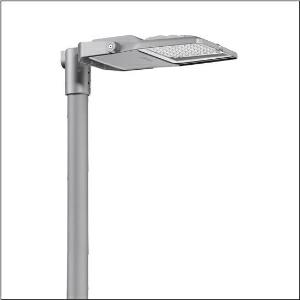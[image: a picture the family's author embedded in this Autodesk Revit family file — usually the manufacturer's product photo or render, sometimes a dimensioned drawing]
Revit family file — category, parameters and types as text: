
# Revit family: floodlight_fl_21_mini___pl61_5xa7775c2c3a_8aba
name_source: partatom
category: Lighting Fixtures
units: mm (PartAtom-declared; Revit-internal decimal feet)

## family parameters
Cut with Voids When Loaded = No
Host = Face
Light Source = No
Part Type = Normal
Room Calculation Point = No
Round Connector Dimension = Use Diameter
Shared = No

## types (1)
- --- (1 x LED, 11960 lm, 89 W, 3000K)
    Apparent Load = 89 VA
    CIE Flux Codes = 33 65 98 100 100
    Color Rendering = 70
    Color Temperature = 3000K
    Default Elevation = 1800 mm
    Description = Floodlight FL 21 mini, floodlight, primary light control with lens, of PMMA, primary optical cover: protective disc, of toughened safety glass, transparent, light distribution: PL61, light emission: direct distribution, installation type: surface-mounted, LED, High Power LED, rated luminous flux: 11.960lm, luminous efficacy: 134lm/W, light colour: 730, colour temperature: 3000K, control: flexible luminous flux parameterisation, time-dependent luminous flux control, constant luminous flux control, overheat protection, pre-setting: logarithmic dimming characteristic, with terminal, 6-pole, mains connection: 220..240V, AC, 50/60Hz, start of lifetime: 89W, end of service life: 94W, reduction: 43W, luminaire housing, of diecast aluminium, powder-coated, Siteco® metallic grey (DB 702S), corrosivity category C5 mid according to DIN EN ISO 12944, sealing non-destructively replaceable, please order mast flange separately, mast bracket, of steel, galvanised, powder-coated, Siteco® metallic grey (DB 702S), Smart Interface above, protection rating (complete): IP66, insulation class (complete): insulation class II (safety insulation), certification: CE, ENEC, VDE, protection symbol: D, impact resistance: IK08, permissible operating ambient temperature: -40..+40°C, permissible operating ambient temperature for outdoor applications: -40..+50°C, standard: DIN EN 12944, LABS conformity tested according to VDMA 24364:2018-05, packaging unit: 1 piece

Light Distribution: PL61
    Height = 70 mm
    Lamp = 1 x LED
    Lamp Light Flux = 11960 lm
    Lamp Power = 89 W
    Lamp count = 1
    Length = 485 mm
    Luminous efficacy = 134 lm/W
    Manufacturer = Siteco
    ModVariant = No
    Model = 5XA7775C2C3A
    Number of Poles = 1
    OnlyDefault = Yes
    Power Factor = 1
    Product Name = Floodlight FL 21 mini | PL61
    Product group = floodlight | pylon annexe
    ProductGroupID = 6200
    Protection Class = Protection class II
    Protection Degree = IP 66
    RLX_Detail_Level = 1
    RLX_Emergency_Light_Flux = 0 lm
    RLX_Emergency_Type = 0
    RLX_Emergency_Type_DB = No
    RlxData = <blob elided: 100877 chars, md5=4cc9cef2>
    Socket = socket
    Standby Power = 0 W
    System Light Flux = 11960 lm
    System Power = 89 W
    Type Comments = factory setting: luminous flux: 100 % | dim-lin: 254 | 456 mA
    Type Image = l_1007125.jpg
    URL = http://relux.com
    VarID = @adj_143171
    Voltage = 0 V
    Weight = 0.00 kg
    Width = 337 mm

## geometry (parser evidence)
native form markers: Blend x4, Sweep x12
no freeform markers — native parametric forms only
